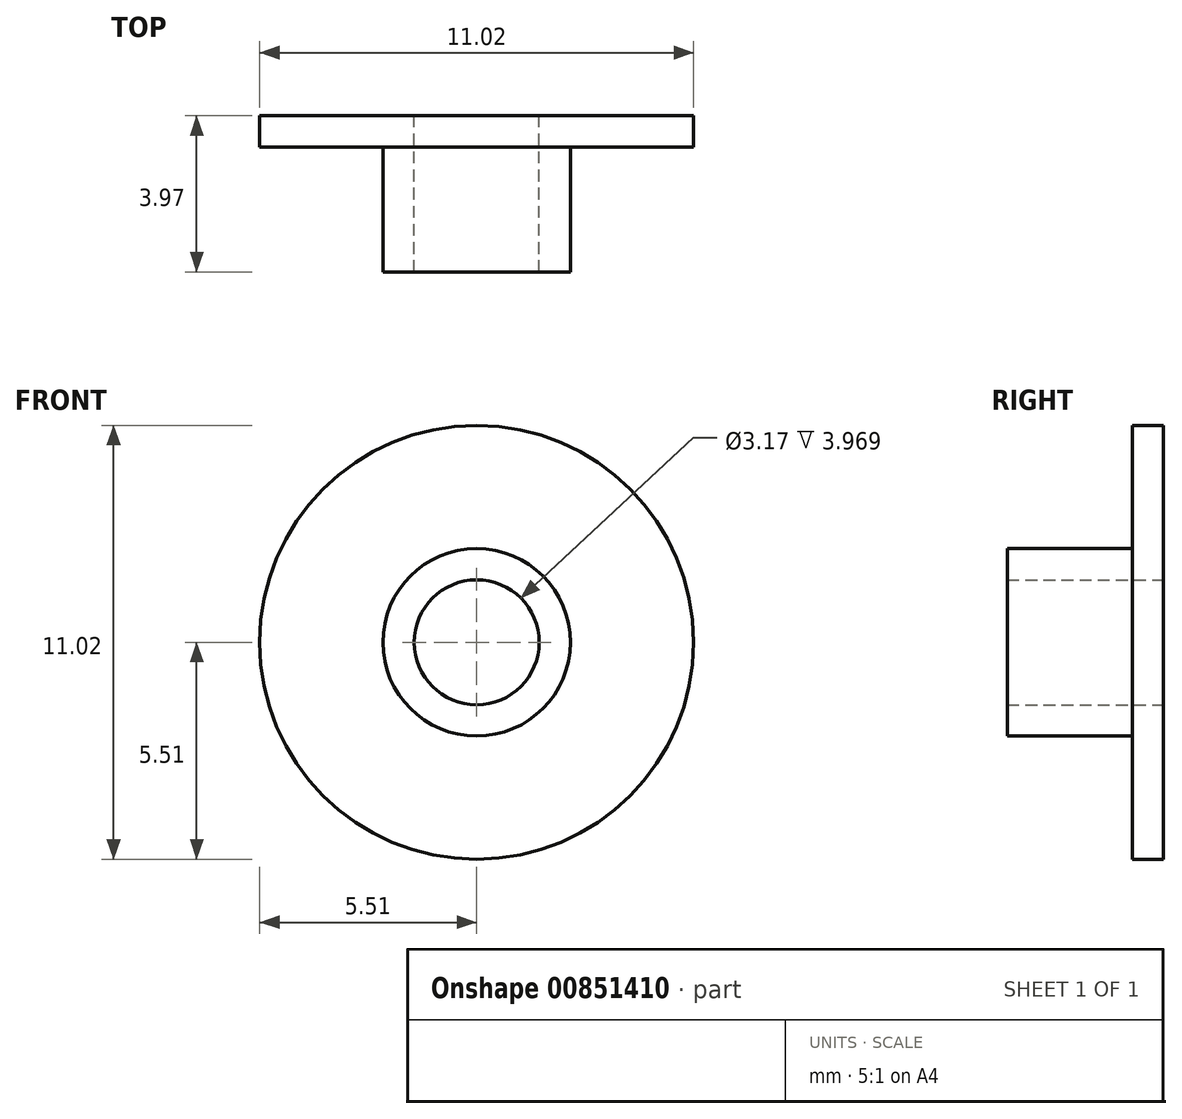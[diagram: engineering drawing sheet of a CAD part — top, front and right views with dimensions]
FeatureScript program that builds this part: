
annotation { "Feature Type Name" : "Feature", "Feature Type Description" : "" }
export const myFeature = defineFeature(function(context is Context, id is Id, definition is map)
    precondition{}
    {
        {
            var Q0;
            Q0=qCreatedBy(makeId("Right.planeOp"),FACE);
            var sketch = newSketch(context, id + "F0", { "sketchPlane" : qUnion([Q0])});
            skLineSegment(sketch, "E0", {"start": v(0, 1.59) * mm, "end": v(0, 2.38) * mm});
            skLineSegment(sketch, "E1", {"start": v(0, 2.38) * mm, "end": v(3.17, 2.38) * mm});
            skLineSegment(sketch, "E2", {"start": v(3.17, 2.38) * mm, "end": v(3.17, 5.51) * mm});
            skLineSegment(sketch, "E3", {"start": v(3.17, 5.51) * mm, "end": v(3.97, 5.51) * mm});
            skLineSegment(sketch, "E4", {"start": v(3.97, 5.51) * mm, "end": v(3.97, 1.59) * mm});
            skLineSegment(sketch, "E5", {"start": v(3.97, 1.59) * mm, "end": v(0, 1.59) * mm});
            skLineSegment(sketch, "E6", {"start": v(0, 0) * mm, "end": v(-3.5, 0) * mm, "construction": true});
            skSolve(sketch);
        }
        {
            var Q0;
            Q0 = qSketchRegion(id + "F0", true);
            var Q1;
            Q1=sQuery(id+"F0.wireOp",EDGE,"E6");
            revolve(context, id + "F1", {"surfaceOperationType" : NewSurfaceOperationType.NEW, "entities" : qUnion([Q0]), "axis" : qUnion([Q1]), "revolveType" : RevolveType.FULL});
        }
    });
